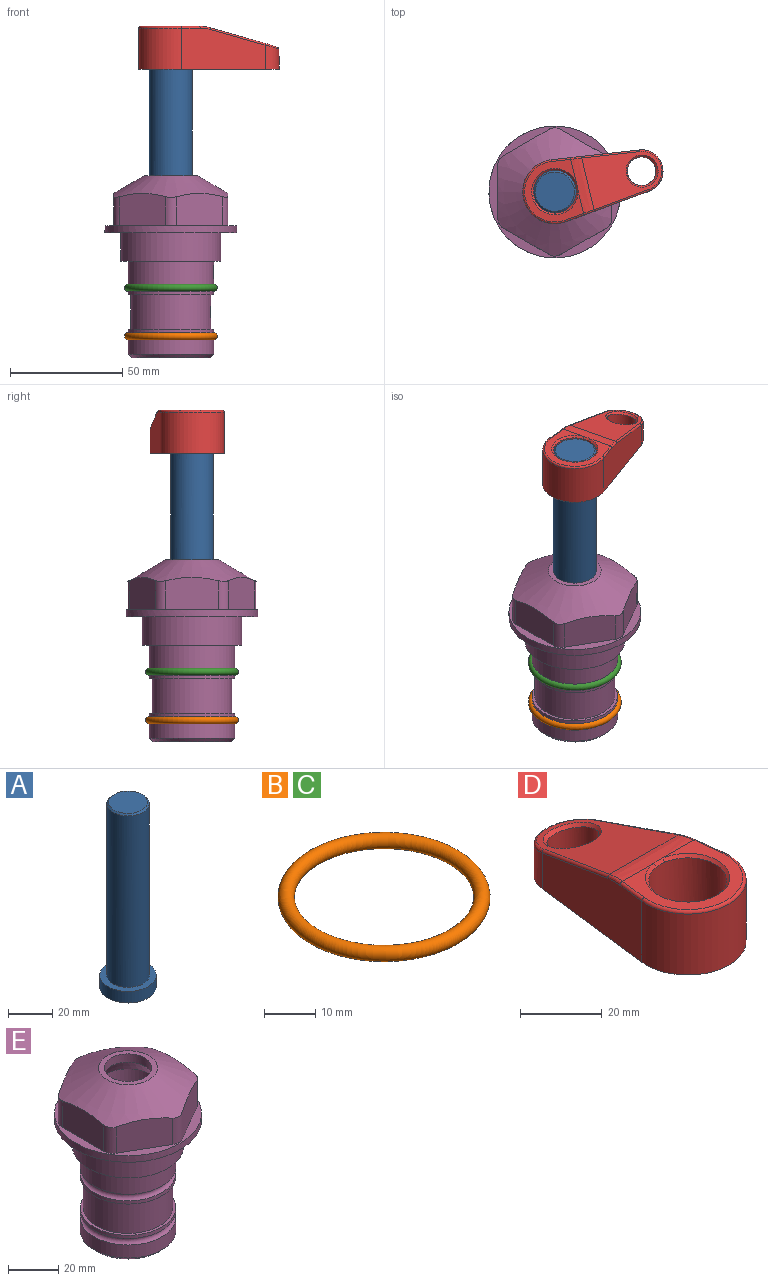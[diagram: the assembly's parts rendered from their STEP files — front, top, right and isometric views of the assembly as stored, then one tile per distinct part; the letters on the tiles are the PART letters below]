
ASSEMBLY  parts=5 mates=4
PART A: 6 faces, bbox 25.4x25.4x101.6 mm
  f0: plane 17.46x17.46mm, normal (0,0,1), area 239.5mm2, adj f5
  f1: plane 25.4x25.4mm, normal (0,0,-1), area 506.7mm2, adj f2
  f2: cylinder r=12.7mm len=25.4mm, axis (0,0,1), area 506.7mm2, adj f1,f3
  f3: plane 25.4x25.4mm, normal (0,0,1), area 221.7mm2, adj f2,f4
  f4: cylinder r=9.53mm len=94.46mm, axis (0,0,1), area 5653mm2, adj f3,f5
  f5: cone r=8.73mm half-angle=45deg, axis (0,0,-1), area 64.4mm2, adj f0,f4
PART B: 1 faces, bbox 44.7x44.7x3.2 mm
  f0: torus R=19.05mm, axis (0,0,1), area 1193.9mm2
PART C: same geometry as B
PART D: 31 faces, bbox 31.7x65.5x19.8 mm
  f0: plane 39.12x18.26mm, normal (0.99,0.12,0), area 612.2mm2, adj f1,f4,f7,f11,f13,f15
  f1: cylinder r=9.53mm len=18.91mm, axis (0,0,-1), area 296.1mm2, adj f0,f2,f7,f17
  f2: plane 39.12x18.26mm, normal (-0.99,0.12,0), area 612.2mm2, adj f1,f4,f7,f12,f14,f16
  f3: cylinder r=6.35mm len=12.7mm, axis (0,0,-1), area 362.4mm2, adj f7,f18
  f4: cylinder r=14.29mm len=28.58mm, axis (0,0,-1), area 882.2mm2, adj f0,f2,f7,f10
  f5: cylinder r=9.53mm len=19.05mm, axis (0,0,-1), area 1092.6mm2, adj f7,f19,f20
  f6: plane 26.99x23.69mm, normal (0,0,1), area 216.2mm2, adj f9,f10,f11,f12,f19
  f7: plane 63.5x28.58mm, normal (0,0,-1), area 661.8mm2, adj f0,f1,f2,f3,f4,f5,f22,f23
  f8: plane 33.52x23.6mm, normal (0,0.26,0.97), area 486mm2, adj f9,f15,f16,f17,f18
  f9: cylinder r=19.05mm len=24.72mm, axis (1,0,0), area 120.4mm2, adj f6,f8,f13,f14,f20
  f10: torus R=13.49mm, axis (0,0,1), area 59mm2, adj f4,f6,f11,f12
  f11: cylinder r=0.79mm len=8.67mm, axis (0.12,-0.99,0), area 10.8mm2, adj f0,f6,f10,f13
  f12: cylinder r=0.79mm len=8.67mm, axis (0.12,0.99,0), area 10.8mm2, adj f2,f6,f10,f14
  f13: bspline ~4.95x1.42mm, area 6.1mm2, adj f0,f9,f11,f15
  f14: bspline ~4.95x1.42mm, area 6.1mm2, adj f2,f9,f12,f16
  f15: cylinder r=0.79mm len=25.95mm, axis (0.12,-0.96,0.26), area 32.9mm2, adj f0,f8,f13,f17
  f16: cylinder r=0.79mm len=25.95mm, axis (0.12,0.96,-0.26), area 32.9mm2, adj f2,f8,f14,f17
  f17: bspline ~18.91x8.38mm, area 30mm2, adj f1,f8,f15,f16
  f18: bspline ~14.29x14.29mm, area 48.3mm2, adj f3,f8
  f19: cone r=9.53mm half-angle=45deg, axis (0,0,1), area 66.5mm2, adj f5,f6,f20
  f20: bspline ~3.22x0.96mm, area 3.5mm2, adj f5,f9,f19
  f21: plane 2.75x2.72mm, normal (0,0,-1), area 2.9mm2, adj f23,f25,f28
  f22: plane 23.05x15.88mm, normal (-0.99,-0.12,0), area 323.6mm2, adj f7,f25,f26,f27,f28,f29
  f23: plane 23.05x15.88mm, normal (0.99,-0.12,0), area 323.6mm2, adj f7,f21,f25,f27,f28,f30
  f24: cylinder r=9.53mm len=10.69mm, axis (0,0,-1), area 114.7mm2, adj f7,f27,f29,f30
  f25: cylinder r=12.7mm len=20.59mm, axis (0,0,-1), area 381.1mm2, adj f7,f21,f22,f23,f26,f28
  f26: plane 2.75x2.72mm, normal (0,0,-1), area 2.9mm2, adj f22,f25,f28
  f27: plane 19.72x18.37mm, normal (0,-0.26,-0.97), area 291.8mm2, adj f22,f23,f24,f28,f29,f30
  f28: cylinder r=15.88mm len=19.92mm, axis (1,0,0), area 54.8mm2, adj f21,f22,f23,f25,f26,f27
  f29: cylinder r=1.59mm len=11mm, axis (0,0,-1), area 34.7mm2, adj f7,f22,f24,f27
  f30: cylinder r=1.59mm len=11mm, axis (0,0,-1), area 34.7mm2, adj f7,f23,f24,f27
PART E: 36 faces, bbox 58.7x58.7x81 mm
  f0: cylinder r=17.78mm len=35.56mm, axis (0,0,1), area 1670.8mm2, adj f23,f24,f31
  f1: cylinder r=19.05mm len=38.1mm, axis (0,0,1), area 1191.9mm2, adj f26,f27,f30
  f2: plane 58.66x58.66mm, normal (0,0,-1), area 1150.6mm2, adj f3,f28
  f3: cylinder r=29.33mm len=58.66mm, axis (0,0,-1), area 585.1mm2, adj f2,f4
  f4: plane 58.66x58.66mm, normal (0,0,1), area 475.9mm2, adj f3,f5,f6,f7,f8,f9,f10,f11
  f5: plane 20.32x14.34mm, normal (-0.5,0.87,0), area 324.4mm2, adj f4,f15,f16,f17
  f6: plane 20.32x14.34mm, normal (0.5,0.87,0), area 324.4mm2, adj f4,f14,f15,f17
  f7: plane 23.48x14.34mm, normal (1,0,0), area 324.4mm2, adj f4,f13,f14,f17
  f8: plane 20.32x14.34mm, normal (0.5,-0.87,0), area 324.4mm2, adj f4,f12,f13,f17
  f9: plane 20.32x14.34mm, normal (-0.5,-0.87,0), area 324.4mm2, adj f4,f11,f12,f17
  f10: plane 23.48x14.34mm, normal (-1,0,0), area 324.4mm2, adj f4,f11,f16,f17
  f11: cylinder r=5.08mm len=12.85mm, axis (0,0,-1), area 67.2mm2, adj f4,f9,f10,f17
  f12: cylinder r=5.08mm len=12.85mm, axis (0,0,-1), area 67.2mm2, adj f4,f8,f9,f17
  f13: cylinder r=5.08mm len=12.85mm, axis (0,0,-1), area 67.2mm2, adj f4,f7,f8,f17
  f14: cylinder r=5.08mm len=12.85mm, axis (0,0,-1), area 67.2mm2, adj f4,f6,f7,f17
  f15: cylinder r=5.08mm len=12.85mm, axis (0,0,-1), area 67.2mm2, adj f4,f5,f6,f17
  f16: cylinder r=5.08mm len=12.85mm, axis (0,0,-1), area 67.2mm2, adj f4,f5,f10,f17
  f17: cone r=11.73mm half-angle=60deg, axis (0,0,-1), area 2071.8mm2, adj f5,f6,f7,f8,f9,f10,f11,f12
  f18: plane 23.46x23.46mm, normal (0,0,1), area 147.4mm2, adj f17,f35
  f19: plane 34.93x34.93mm, normal (0,0,-1), area 958mm2, adj f29
  f20: cylinder r=19.05mm len=38.1mm, axis (0,0,1), area 760.1mm2, adj f21,f29
  f21: torus R=19.05mm, axis (0,0,1), area 565.3mm2, adj f20,f22
  f22: cylinder r=19.05mm len=38.1mm, axis (0,0,1), area 190mm2, adj f21,f23
  f23: plane 38.1x38.1mm, normal (0,0,1), area 146.9mm2, adj f0,f22
  f24: plane 38.1x38.1mm, normal (0,0,-1), area 146.9mm2, adj f0,f25
  f25: cylinder r=19.05mm len=38.1mm, axis (0,0,1), area 190mm2, adj f24,f26
  f26: torus R=19.05mm, axis (0,0,1), area 565.3mm2, adj f1,f25
  f27: plane 44.45x44.45mm, normal (0,0,-1), area 411.7mm2, adj f1,f28
  f28: cylinder r=22.23mm len=44.45mm, axis (0,0,1), area 1773.5mm2, adj f2,f27
  f29: cone r=19.05mm half-angle=45deg, axis (0,0,1), area 257.5mm2, adj f19,f20
  f30: cylinder r=3.17mm len=6.75mm, axis (-1,0,0), area 128mm2, adj f1,f33
  f31: cylinder r=3.17mm len=6.35mm, axis (-1,0,0), area 102.5mm2, adj f0,f33
  f32: plane 25.4x25.4mm, normal (0,0,1), area 506.7mm2, adj f33
  f33: cylinder r=12.7mm len=66.42mm, axis (0,0,-1), area 5236.2mm2, adj f30,f31,f32,f34
  f34: cone r=9.53mm half-angle=30deg, axis (0,0,-1), area 443.4mm2, adj f33,f35
  f35: cylinder r=9.53mm len=19.05mm, axis (0,0,-1), area 240.9mm2, adj f18,f34
PLACE A rot(axis=(0,0,-1),76.7deg) t=(0,0,27.55)mm
PLACE B t=(0,0,-21.59)mm
PLACE C at identity
PLACE D rot(axis=(0,0,-1),76.7deg) t=(0,0,28.35)mm
PLACE E at identity fixed
MATE cylindrical E.f0 <-> A.f2  axis (0,0,1) through (0,0,-50.55)mm
MATE fastened D.f4 <-> A.f2  axis (0,0,-1) through (0,0,91.05)mm
MATE fastened B.f0 <-> E.f0  axis (0,0,1) through (0,0,-46.1)mm
MATE fastened C.f0 <-> E.f0  axis (0,0,1) through (0,0,-24.51)mm
